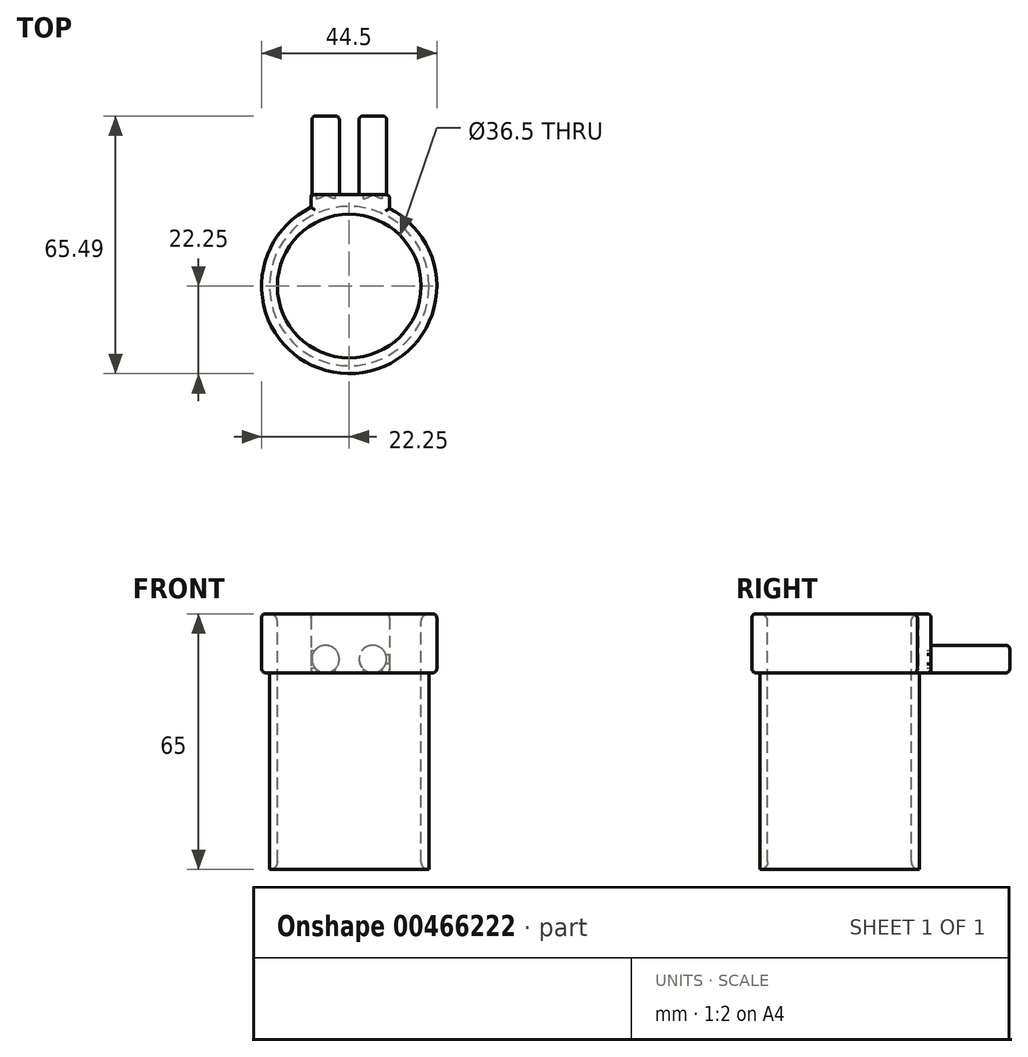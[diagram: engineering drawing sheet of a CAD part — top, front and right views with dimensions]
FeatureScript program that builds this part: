
annotation { "Feature Type Name" : "Feature", "Feature Type Description" : "" }
export const myFeature = defineFeature(function(context is Context, id is Id, definition is map)
    precondition{}
    {
        {
            var Q0;
            Q0=qCreatedBy(makeId("Top.planeOp"),FACE);
            var sketch = newSketch(context, id + "F0", { "sketchPlane" : qUnion([Q0])});
            skArc(sketch, "E0", {"start": v(-9.71, 20.02) * mm, "mid": v(-0.32, -22.25) * mm, "end": v(10.29, 19.73) * mm});
            skCircle(sketch, "E1", {"center": v(0, 0) * mm, "radius": 20.25 * mm});
            skLineSegment(sketch, "E2.top", {"start": v(-9.71, 23.24) * mm, "end": v(10.29, 23.24) * mm});
            skLineSegment(sketch, "E2.left", {"start": v(-9.71, 20.02) * mm, "end": v(-9.71, 23.24) * mm});
            skLineSegment(sketch, "E2.right", {"start": v(10.29, 19.73) * mm, "end": v(10.29, 23.24) * mm});
            skCircle(sketch, "E3", {"center": v(0, 0) * mm, "radius": 18.25 * mm});
            skSolve(sketch);
        }
        {
            var Q0;
            Q0=makeQuery(id+"F0.imprint","IMPRINT",FACE,{"disambiguationData":[TD([[makeQuery(id+"F0.imprint","IMPRINT",EDGE,{"derivedFrom":sQuery(id+"F0.wireOp",EDGE,"E0")}),1.0]])]});
            extrude(context, id + "F1", {"entities" : qUnion([Q0]), "depth" : 15 * mm});
        }
        {
            var Q0;
            Q0=makeQuery(id+"F1.opExtrude","SWEPT_FACE",FACE,{"disambiguationData":[OSD([sQuery(id+"F0.wireOp",EDGE,"E2.top")])]});
            cPlane(context, id + "F2", {"entities" : qUnion([Q0]), "cplaneType" : CPlaneType.OFFSET, "offset" : 0 * mm, "width" : 150 * mm, "height" : 150 * mm});
        }
        {
            var Q0;
            Q0=qCreatedBy(id+"F2.planeOp",FACE);
            var sketch = newSketch(context, id + "F3", { "sketchPlane" : qUnion([Q0])});
            skCircle(sketch, "E4", {"center": v(-6, 3.5) * mm, "radius": 3.5 * mm});
            skCircle(sketch, "E5", {"center": v(6, 3.5) * mm, "radius": 3.5 * mm});
            skSolve(sketch);
        }
        {
            var Q0;
            Q0=makeQuery(id+"F3.imprint","IMPRINT",FACE,{"disambiguationData":[TD([[makeQuery(id+"F3.imprint","IMPRINT",EDGE,{"derivedFrom":sQuery(id+"F3.wireOp",EDGE,"E4")}),1.0]])]});
            var Q1;
            Q1=makeQuery(id+"F3.imprint","IMPRINT",FACE,{"disambiguationData":[TD([[makeQuery(id+"F3.imprint","IMPRINT",EDGE,{"derivedFrom":sQuery(id+"F3.wireOp",EDGE,"E5")}),1.0]])]});
            extrude(context, id + "F4", {"entities" : qUnion([Q0, Q1]), "operationType" : NewBodyOperationType.ADD, "depth" : 20 * mm, "hasSecondDirection" : true, "secondDirectionOppositeDirection" : true, "secondDirectionDepth" : 3 * mm});
        }
        {
            var Q0;
            Q0=makeQuery(id+"F1.opExtrude","CAP_EDGE",EDGE,{"disambiguationData":[OSD([sQuery(id+"F0.wireOp",EDGE,"E0")])],"isStart":true});
            var Q1;
            Q1=makeQuery(id+"F1.opExtrude","CAP_EDGE",EDGE,{"disambiguationData":[OSD([sQuery(id+"F0.wireOp",EDGE,"E0")])],"isStart":false});
            var Q2;
            Q2=makeQuery(id+"F1.opExtrude","SWEPT_EDGE",EDGE,{"disambiguationData":[OSD([sQuery(id+"F0.wireOp",EDGE,"E2.top"),sQuery(id+"F0.wireOp",EDGE,"E2.left")])]});
            var Q3;
            Q3=makeQuery(id+"F1.opExtrude","CAP_EDGE",EDGE,{"disambiguationData":[OSD([sQuery(id+"F0.wireOp",EDGE,"E2.top")])],"isStart":false});
            var Q4;
            Q4=makeQuery(id+"F1.opExtrude","SWEPT_EDGE",EDGE,{"disambiguationData":[OSD([sQuery(id+"F0.wireOp",EDGE,"E2.top"),sQuery(id+"F0.wireOp",EDGE,"E2.right")])]});
            var Q5;
            Q5=makeQuery(id+"F1.opExtrude","CAP_EDGE",EDGE,{"disambiguationData":[OSD([sQuery(id+"F0.wireOp",EDGE,"E2.top")])],"isStart":true});
            var Q6;
            Q6=makeQuery(id+"F1.opExtrude","CAP_EDGE",EDGE,{"disambiguationData":[OSD([sQuery(id+"F0.wireOp",EDGE,"E2.left")])],"isStart":true});
            var Q7;
            Q7=makeQuery(id+"F1.opExtrude","CAP_EDGE",EDGE,{"disambiguationData":[OSD([sQuery(id+"F0.wireOp",EDGE,"E2.left")])],"isStart":false});
            var Q8;
            Q8=makeQuery(id+"F1.opExtrude","CAP_EDGE",EDGE,{"disambiguationData":[OSD([sQuery(id+"F0.wireOp",EDGE,"E2.right")])],"isStart":false});
            var Q9;
            Q9=makeQuery(id+"F1.opExtrude","CAP_EDGE",EDGE,{"disambiguationData":[OSD([sQuery(id+"F0.wireOp",EDGE,"E2.right")])],"isStart":true});
            var Q10;
            Q10=makeQuery(id+"F4.opExtrude","CAP_EDGE",EDGE,{"disambiguationData":[OSD([sQuery(id+"F3.wireOp",EDGE,"E4")])],"isStart":false});
            var Q11;
            Q11=makeQuery(id+"F4.opExtrude","CAP_EDGE",EDGE,{"disambiguationData":[OSD([sQuery(id+"F3.wireOp",EDGE,"E5")])],"isStart":false});
            fillet(context, id + "F5", {"entities" : qUnion([Q0, Q1, Q2, Q3, Q4, Q5, Q6, Q7, Q8, Q9, Q10, Q11]), "radius" : 1 * mm, "tangentPropagation" : true, "allowEdgeOverflow" : false});
        }
        {
            var Q0;
            Q0=makeQuery(id+"F0.imprint","IMPRINT",FACE,{"disambiguationData":[TD([[makeQuery(id+"F0.imprint","IMPRINT",EDGE,{"derivedFrom":sQuery(id+"F0.wireOp",EDGE,"E1")}),1.0]])]});
            extrude(context, id + "F6", {"entities" : qUnion([Q0]), "operationType" : NewBodyOperationType.ADD, "oppositeDirection" : true, "depth" : 50 * mm, "hasSecondDirection" : true, "secondDirectionOppositeDirection" : false, "secondDirectionDepth" : 15 * mm, "offsetDistance" : 25 * mm});
        }
        {
            var Q0;
            Q0=makeQuery(id+"F6.opExtrude","CAP_EDGE",EDGE,{"disambiguationData":[OSD([sQuery(id+"F0.wireOp",EDGE,"E3")])],"isStart":true});
            var Q1;
            Q1=makeQuery(id+"F6.opExtrude","CAP_EDGE",EDGE,{"disambiguationData":[OSD([sQuery(id+"F0.wireOp",EDGE,"E3")])],"isStart":false});
            fillet(context, id + "F7", {"entities" : qUnion([Q0, Q1]), "radius" : 2 * mm, "tangentPropagation" : true, "allowEdgeOverflow" : false});
        }
    });
